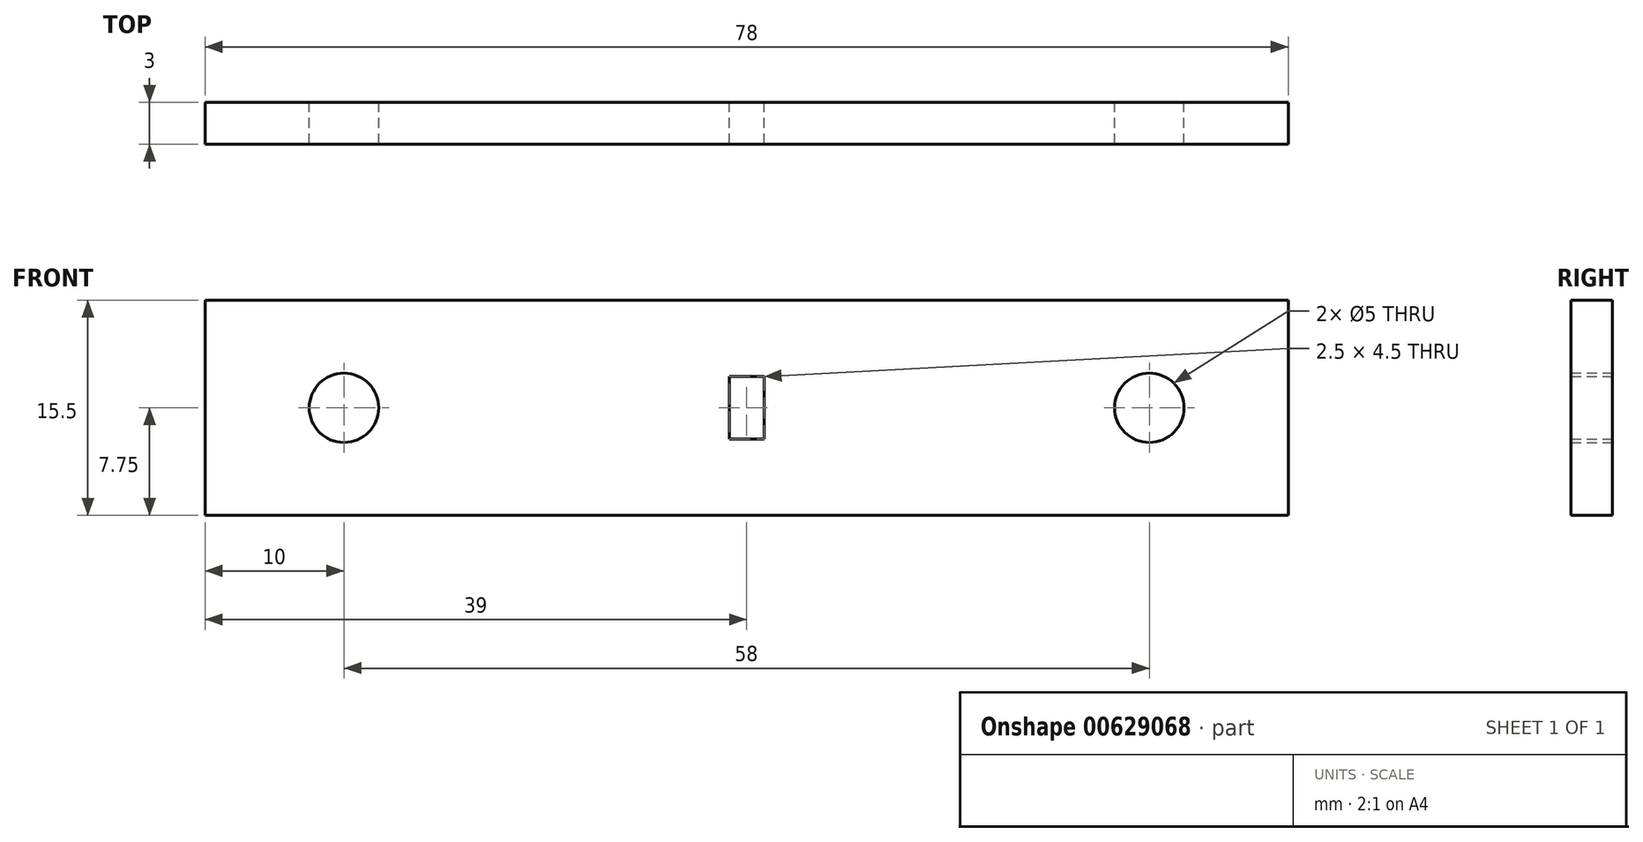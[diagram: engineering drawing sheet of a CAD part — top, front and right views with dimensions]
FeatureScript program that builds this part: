
annotation { "Feature Type Name" : "Feature", "Feature Type Description" : "" }
export const myFeature = defineFeature(function(context is Context, id is Id, definition is map)
    precondition{}
    {
        {
            var Q0;
            Q0=qCreatedBy(makeId("Front.planeOp"),FACE);
            var sketch = newSketch(context, id + "F0", { "sketchPlane" : qUnion([Q0])});
            skLineSegment(sketch, "E0", {"start": v(0, 15.87) * mm, "end": v(0, -16.61) * mm, "construction": true});
            skLineSegment(sketch, "E1", {"start": v(-55.25, 0) * mm, "end": v(63.12, 0) * mm, "construction": true});
            skLineSegment(sketch, "E2.bottom", {"start": v(-39, 7.75) * mm, "end": v(39, 7.75) * mm});
            skLineSegment(sketch, "E2.top", {"start": v(-39, -7.75) * mm, "end": v(39, -7.75) * mm});
            skLineSegment(sketch, "E2.left", {"start": v(-39, 7.75) * mm, "end": v(-39, -7.75) * mm});
            skLineSegment(sketch, "E2.right", {"start": v(39, 7.75) * mm, "end": v(39, -7.75) * mm});
            skCircle(sketch, "E3", {"center": v(-29, 0) * mm, "radius": 2.5 * mm});
            skCircle(sketch, "E4", {"center": v(29, 0) * mm, "radius": 2.5 * mm});
            skLineSegment(sketch, "E5.bottom", {"start": v(-1.25, 2.25) * mm, "end": v(1.25, 2.25) * mm});
            skLineSegment(sketch, "E5.top", {"start": v(-1.25, -2.25) * mm, "end": v(1.25, -2.25) * mm});
            skLineSegment(sketch, "E5.left", {"start": v(-1.25, 2.25) * mm, "end": v(-1.25, -2.25) * mm});
            skLineSegment(sketch, "E5.right", {"start": v(1.25, 2.25) * mm, "end": v(1.25, -2.25) * mm});
            skSolve(sketch);
        }
        {
            var Q0;
            Q0 = qSketchRegion(id + "F0", true);
            extrude(context, id + "F1", {"entities" : qUnion([Q0]), "endBound" : BoundingType.SYMMETRIC, "depth" : 3 * mm, "offsetDistance" : 25 * mm});
        }
    });
